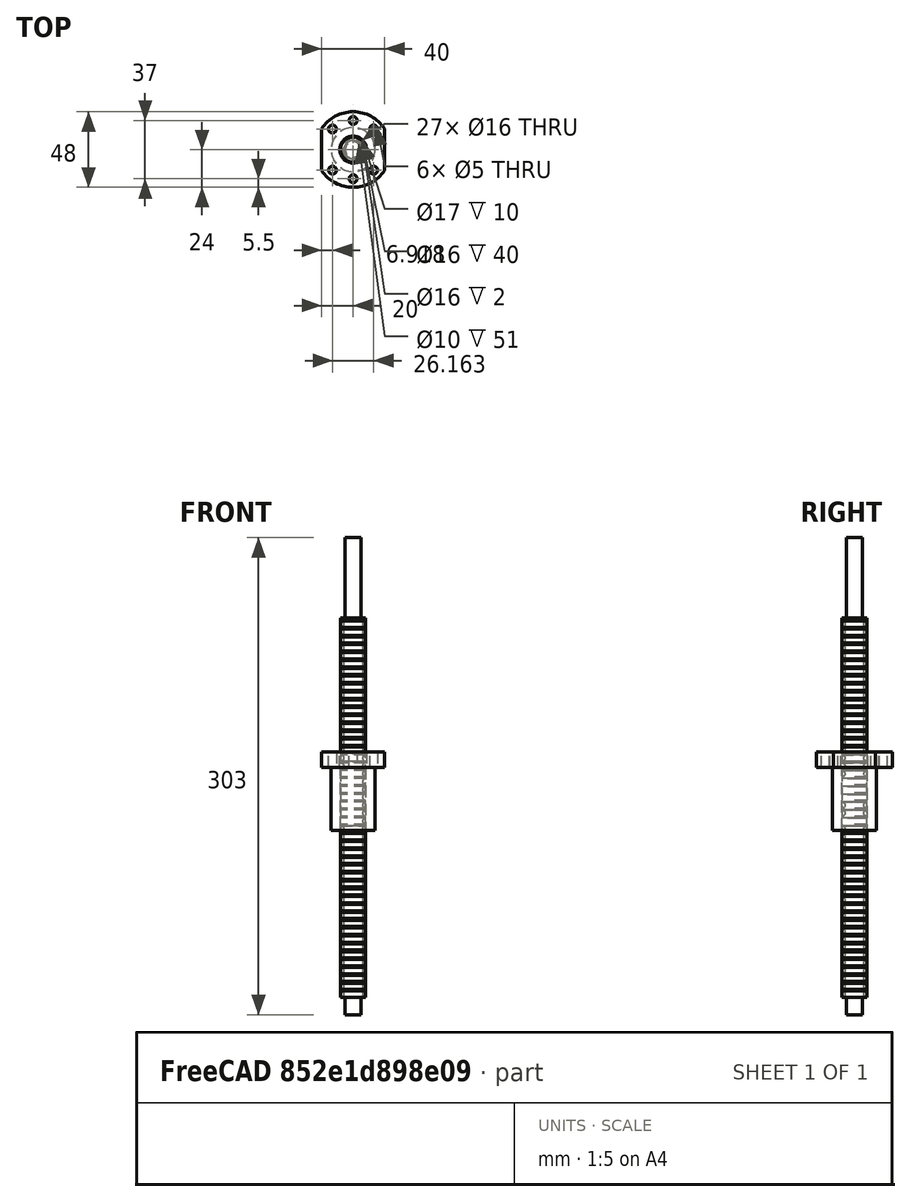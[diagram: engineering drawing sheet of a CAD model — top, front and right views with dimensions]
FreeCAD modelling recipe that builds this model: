
FCSTD DOCUMENT  (FreeCAD 0.14R3702 (Git))
Label: simple_ballscrew_300mm
License: CC-BY 3.0
LicenseURL: http://creativecommons.org/licenses/by/3.0/
objects: Sketcher::SketchObject×2, PartDesign::Pad×2, Part::Feature×1, Part::Torus×1, Part::FeaturePython×1, Part::Cut×1, Part::MultiFuse×1
note: 11 computed .brp shape members not serialized (recipe doc carries the construction recipe); baked Part::Feature solids carry a one-line shape summary decoded from their .brp

FEATURE [Sketcher::SketchObject] Sketch
  sketch-geometry (1):
    g0: Circle CenterX=0 CenterY=0 CenterZ=0 NormalX=0 NormalY=0 NormalZ=1 Radius=8
  constraints (2):
    c: Coincident(g0,g-1)
    c: Radius(g0) = 8
FEATURE [PartDesign::Pad] Pad001
  Length = 241
  Length2 = 1
  Sketch = -> Sketch
  Type = 0
FEATURE [Sketcher::SketchObject] Sketch001
  Placement = pos=(0,0,0) rot=(1,0,0;3.14159rad)
  Support = -> Pad001 [Face2]
  sketch-geometry (1):
    g0: Circle CenterX=0 CenterY=0 CenterZ=0 NormalX=0 NormalY=0 NormalZ=1 Radius=5
  constraints (2):
    c: Coincident(g0,g-1)
    c: Radius(g0) = 5
FEATURE [PartDesign::Pad] Pad002  label="Pad004"
  Length = 11
  Length2 = 292
  Sketch = -> Sketch001
  Type = 4
FEATURE [Part::Feature] Pad003  label="Pad002"
  Placement = pos=(4.4252e-08,-2.18247e-05,156.004) rot=(1,0,0;3.14159rad)
  shape: bbox 40 x 48 x 50 mm, 17 faces (baked)
FEATURE [Part::Torus] Torus
  Angle1 = -180
  Angle2 = 180
  Angle3 = 360
  Placement = pos=(0,0,2) rot=(0,0,1;0rad)
  Radius1 = 8
  Radius2 = 2
FEATURE [Part::FeaturePython] Array  # Draft array (typed FeaturePython)
  Angle = 360
  ArrayType = 0
  Axis = (0,0,1)
  Base = -> Torus
  Center = (0,0,0)
  IntervalX = (1,0,0)
  IntervalY = (0,1,0)
  IntervalZ = (0,0,5)
  NumberPolar = 1
  NumberX = 1
  NumberY = 1
  NumberZ = 48
FEATURE [Part::Cut] Cut
  Base = -> Pad002
  Tool = -> Array
FEATURE [Part::MultiFuse] Fusion
  Shapes = -> [Pad003,Cut]
